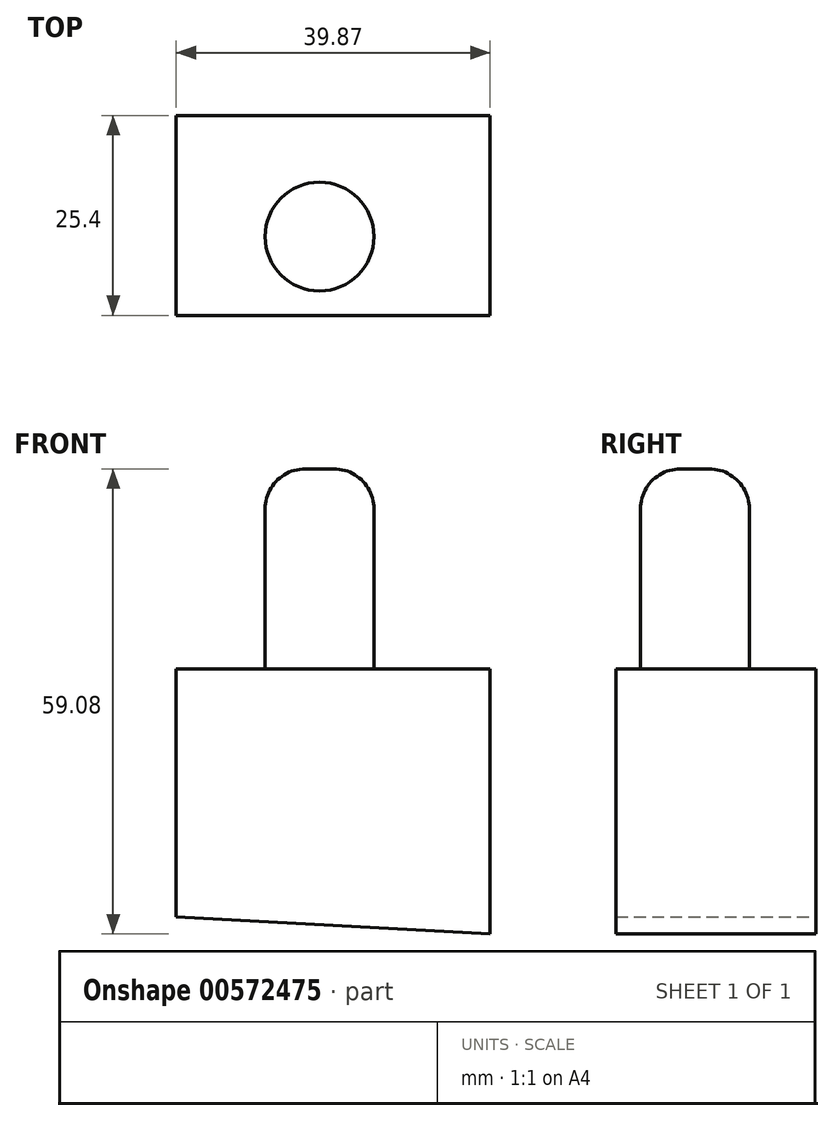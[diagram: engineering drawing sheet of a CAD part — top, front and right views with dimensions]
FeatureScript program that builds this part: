
annotation { "Feature Type Name" : "Feature", "Feature Type Description" : "" }
export const myFeature = defineFeature(function(context is Context, id is Id, definition is map)
    precondition{}
    {
        {
            var Q0;
            Q0=qCreatedBy(makeId("Front.planeOp"),FACE);
            var sketch = newSketch(context, id + "F0", { "sketchPlane" : qUnion([Q0])});
            skLineSegment(sketch, "E0", {"start": v(-74.83, 20.46) * mm, "end": v(-74.83, 51.98) * mm});
            skLineSegment(sketch, "E1", {"start": v(-74.83, 51.98) * mm, "end": v(-34.96, 51.98) * mm});
            skLineSegment(sketch, "E2", {"start": v(-34.96, 51.98) * mm, "end": v(-34.96, 18.3) * mm});
            skLineSegment(sketch, "E3", {"start": v(-34.96, 18.3) * mm, "end": v(-74.83, 20.46) * mm});
            skSolve(sketch);
        }
        {
            var Q0;
            Q0=makeQuery(id+"F0.imprint","IMPRINT",FACE,{"disambiguationData":[TD([[makeQuery(id+"F0.imprint","IMPRINT",EDGE,{"derivedFrom":sQuery(id+"F0.wireOp",EDGE,"E0")}),-1.0]])]});
            extrude(context, id + "F1", {"entities" : qUnion([Q0]), "depth" : 25.4 * mm, "offsetDistance" : 25.4 * mm});
        }
        {
            var Q0;
            Q0=makeQuery(id+"F1.opExtrude","SWEPT_FACE",FACE,{"disambiguationData":[OSD([sQuery(id+"F0.wireOp",EDGE,"E1")])]});
            var sketch = newSketch(context, id + "F2", { "sketchPlane" : qUnion([Q0])});
            skCircle(sketch, "E4", {"center": v(-56.63, -15.39) * mm, "radius": 6.92 * mm});
            skSolve(sketch);
        }
        {
            var Q0;
            Q0=makeQuery(id+"F2.imprint","IMPRINT",FACE,{"disambiguationData":[TD([[makeQuery(id+"F2.imprint","IMPRINT",EDGE,{"derivedFrom":sQuery(id+"F2.wireOp",EDGE,"E4")}),1.0]])]});
            extrude(context, id + "F3", {"entities" : qUnion([Q0]), "operationType" : NewBodyOperationType.ADD, "depth" : 25.4 * mm, "offsetDistance" : 25.4 * mm});
        }
        {
            var Q0;
            Q0=makeQuery(id+"F3.opExtrude","CAP_EDGE",EDGE,{"disambiguationData":[OSD([sQuery(id+"F2.wireOp",EDGE,"E4")])],"isStart":false});
            fillet(context, id + "F4", {"entities" : qUnion([Q0]), "radius" : 5.08 * mm, "tangentPropagation" : true, "allowEdgeOverflow" : false});
        }
    });
